FCSTD DOCUMENT  (FreeCAD 0.20R29177 (Git))
Label: micro switch
License: All rights reserved
LicenseURL: http://en.wikipedia.org/wiki/All_rights_reserved
objects: Sketcher::SketchObject×1, PartDesign::Body×1
note: 2 computed .brp shape members not serialized (recipe doc carries the construction recipe); baked Part::Feature solids carry a one-line shape summary decoded from their .brp

FEATURE [Sketcher::SketchObject] Sketch
  FullyConstrained = true
  MapMode = 5
  Support = -> [XY_Plane]
  sketch-geometry (8):
    g0: LineSegment StartX=19.8 StartY=9.5 StartZ=0 EndX=19.8 EndY=0 EndZ=0
    g1: LineSegment StartX=19.8 StartY=0 StartZ=0 EndX=0 EndY=0 EndZ=0
    g2: LineSegment StartX=0 StartY=0 StartZ=0 EndX=0 EndY=10.2 EndZ=0
    g3: LineSegment StartX=0 StartY=10.2 StartZ=0 EndX=8.8 EndY=10.2 EndZ=0
    g4: LineSegment StartX=8.8 StartY=10.2 StartZ=0 EndX=10.4 EndY=9.5 EndZ=0
    g5: LineSegment StartX=10.4 StartY=9.5 StartZ=0 EndX=19.8 EndY=9.5 EndZ=0
    g6: Circle CenterX=5.1 CenterY=2.2 CenterZ=0 NormalX=0 NormalY=0 NormalZ=1 AngleXU=0 Radius=1.2
    g7: Circle CenterX=14.7 CenterY=2.2 CenterZ=0 NormalX=0 NormalY=0 NormalZ=1 AngleXU=0 Radius=1.2
  constraints (24):
    c: Coincident(g0,g1)
    c: Coincident(g1,g2)
    c: Horizontal(g1)
    c: Vertical(g0)
    c: Vertical(g2)
    c: Coincident(g2,g3)
    c: Horizontal(g3)
    c: Coincident(g3,g4)
    c: Coincident(g4,g5)
    c: Coincident(g5,g0)
    c: Horizontal(g5)
    c: Distance(g0) = 9.5
    c: Distance(g2) = 10.2
    c: Distance(g1) = 19.8
    c: Distance(g5) = 9.4
    c: Coincident(g1,g-1)
    c: Distance(g3) = 8.8
    c: Diameter(g6) = 2.4
    c: Diameter(g7) = 2.4
    c: Distance(g6,g1) = 2.2
    c: Horizontal(g6,g7)
    c: Distance(g6,g2) = 5.1
    c: Distance(g7,g0) = 5.1
    c: Distance(g6,g7) = 9.6
FEATURE [PartDesign::Body] Body
  Group = -> [Sketch]
  Origin = -> Origin
